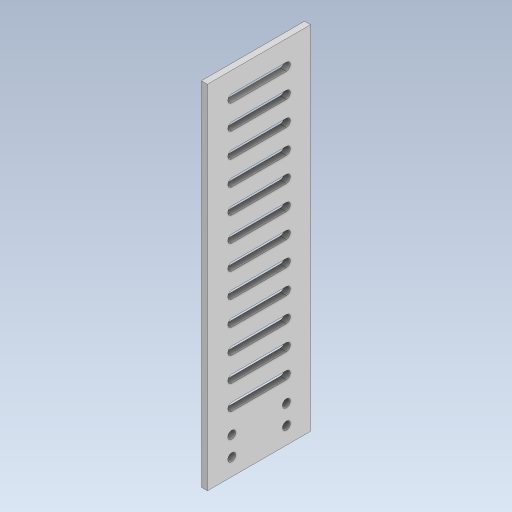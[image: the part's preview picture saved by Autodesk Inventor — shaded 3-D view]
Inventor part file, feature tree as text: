
AUTODESK INVENTOR PART (.ipt)
format: ipt  version: 2023.5 (Build 275446000, 446)  size: 425,984 bytes
history: native  units: mm
features: extrude x1, sketch x1
ambient origin geometry x8: Origin, YZ Plane, XZ Plane, XY Plane, X Axis, Y Axis, Z Axis, Center Point
bodies: Solid1 (feature_tree)
feature tree (2):
  extrude  "Extrusion1"  Depth=3.3mm
  sketch  "Sketch1"  dims[d1=3.3mm d3=3.3mm d5=3.3mm d6=10.0mm d7=10.0mm d9=3.3mm d11=120.0mm d13=10.0mm d14=10.0mm d16=10.0mm d18=2.5mm d19=0.0mm d20=15.0mm d22=7.0mm d23=7.0mm d24=8.0mm d25=3.3mm d26=8.0mm d27=8.0mm]
